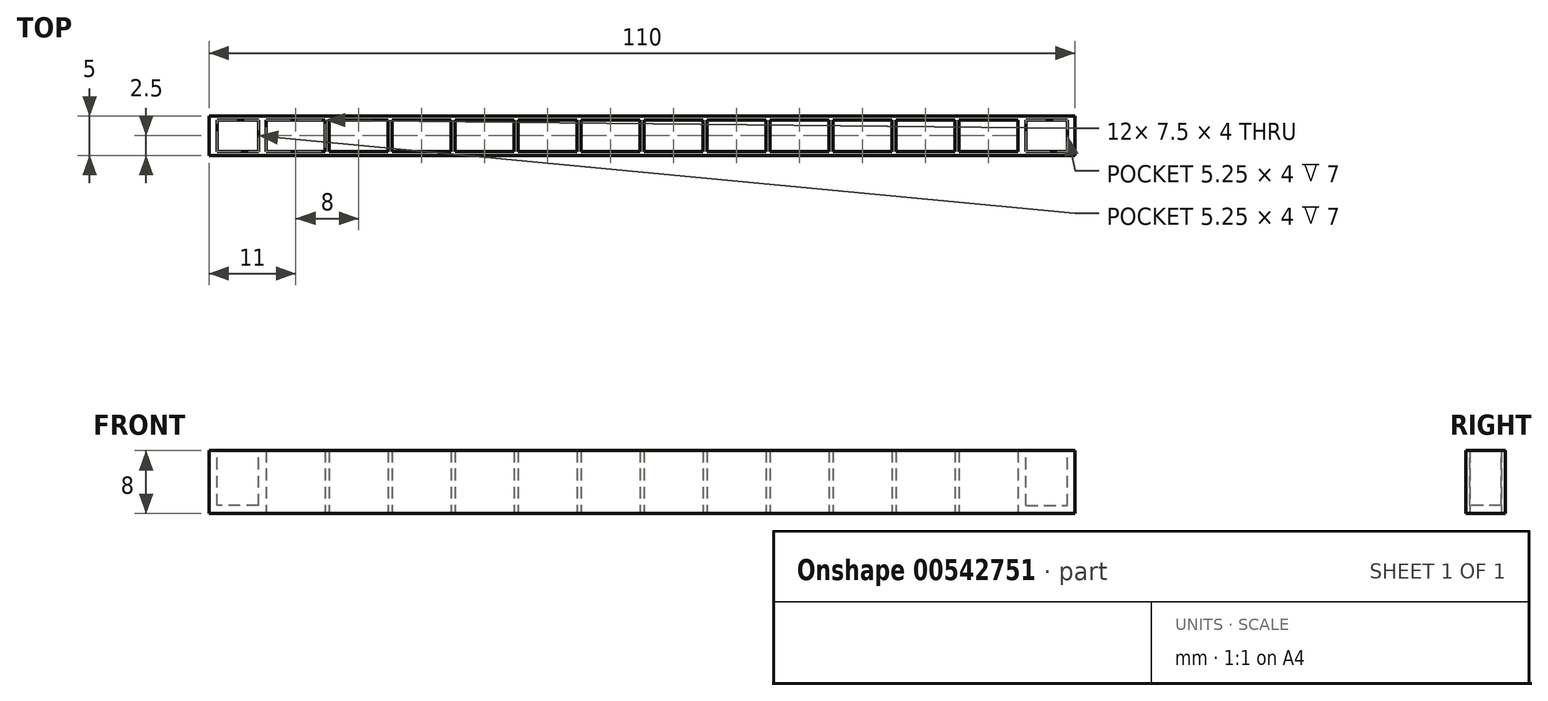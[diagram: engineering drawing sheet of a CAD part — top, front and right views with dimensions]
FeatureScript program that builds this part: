
annotation { "Feature Type Name" : "Feature", "Feature Type Description" : "" }
export const myFeature = defineFeature(function(context is Context, id is Id, definition is map)
    precondition{}
    {
        {
            var Q0;
            Q0=qCreatedBy(makeId("Top.planeOp"),FACE);
            var sketch = newSketch(context, id + "F0", { "sketchPlane" : qUnion([Q0])});
            skLineSegment(sketch, "E0.bottom", {"start": v(-47.75, 2) * mm, "end": v(-40.25, 2) * mm});
            skLineSegment(sketch, "E0.top", {"start": v(-47.75, -2) * mm, "end": v(-40.25, -2) * mm});
            skLineSegment(sketch, "E0.left", {"start": v(-47.75, 2) * mm, "end": v(-47.75, -2) * mm});
            skLineSegment(sketch, "E0.right", {"start": v(-40.25, 2) * mm, "end": v(-40.25, -2) * mm});
            skLineSegment(sketch, "E1.1.0.0", {"start": v(-39.75, 2) * mm, "end": v(-39.75, -2) * mm});
            skLineSegment(sketch, "E1.1.0.1", {"start": v(-39.75, 2) * mm, "end": v(-32.25, 2) * mm});
            skLineSegment(sketch, "E1.1.0.2", {"start": v(-32.25, 2) * mm, "end": v(-32.25, -2) * mm});
            skLineSegment(sketch, "E1.1.0.3", {"start": v(-39.75, -2) * mm, "end": v(-32.25, -2) * mm});
            skLineSegment(sketch, "E1.2.0.0", {"start": v(-31.75, 2) * mm, "end": v(-31.75, -2) * mm});
            skLineSegment(sketch, "E1.2.0.1", {"start": v(-31.75, 2) * mm, "end": v(-24.25, 2) * mm});
            skLineSegment(sketch, "E1.2.0.2", {"start": v(-24.25, 2) * mm, "end": v(-24.25, -2) * mm});
            skLineSegment(sketch, "E1.2.0.3", {"start": v(-31.75, -2) * mm, "end": v(-24.25, -2) * mm});
            skLineSegment(sketch, "E1.3.0.0", {"start": v(-23.75, 2) * mm, "end": v(-23.75, -2) * mm});
            skLineSegment(sketch, "E1.3.0.1", {"start": v(-23.75, 2) * mm, "end": v(-16.25, 2) * mm});
            skLineSegment(sketch, "E1.3.0.2", {"start": v(-16.25, 2) * mm, "end": v(-16.25, -2) * mm});
            skLineSegment(sketch, "E1.3.0.3", {"start": v(-23.75, -2) * mm, "end": v(-16.25, -2) * mm});
            skLineSegment(sketch, "E1.4.0.0", {"start": v(-15.75, 2) * mm, "end": v(-15.75, -2) * mm});
            skLineSegment(sketch, "E1.4.0.1", {"start": v(-15.75, 2) * mm, "end": v(-8.25, 2) * mm});
            skLineSegment(sketch, "E1.4.0.2", {"start": v(-8.25, 2) * mm, "end": v(-8.25, -2) * mm});
            skLineSegment(sketch, "E1.4.0.3", {"start": v(-15.75, -2) * mm, "end": v(-8.25, -2) * mm});
            skLineSegment(sketch, "E1.5.0.0", {"start": v(-7.75, 2) * mm, "end": v(-7.75, -2) * mm});
            skLineSegment(sketch, "E1.5.0.1", {"start": v(-7.75, 2) * mm, "end": v(-0.25, 2) * mm});
            skLineSegment(sketch, "E1.5.0.2", {"start": v(-0.25, 2) * mm, "end": v(-0.25, -2) * mm});
            skLineSegment(sketch, "E1.5.0.3", {"start": v(-7.75, -2) * mm, "end": v(-0.25, -2) * mm});
            skLineSegment(sketch, "E1.6.0.0", {"start": v(0.25, 2) * mm, "end": v(0.25, -2) * mm});
            skLineSegment(sketch, "E1.6.0.1", {"start": v(0.25, 2) * mm, "end": v(7.75, 2) * mm});
            skLineSegment(sketch, "E1.6.0.2", {"start": v(7.75, 2) * mm, "end": v(7.75, -2) * mm});
            skLineSegment(sketch, "E1.6.0.3", {"start": v(0.25, -2) * mm, "end": v(7.75, -2) * mm});
            skLineSegment(sketch, "E1.7.0.0", {"start": v(8.25, 2) * mm, "end": v(8.25, -2) * mm});
            skLineSegment(sketch, "E1.7.0.1", {"start": v(8.25, 2) * mm, "end": v(15.75, 2) * mm});
            skLineSegment(sketch, "E1.7.0.2", {"start": v(15.75, 2) * mm, "end": v(15.75, -2) * mm});
            skLineSegment(sketch, "E1.7.0.3", {"start": v(8.25, -2) * mm, "end": v(15.75, -2) * mm});
            skLineSegment(sketch, "E1.8.0.0", {"start": v(16.25, 2) * mm, "end": v(16.25, -2) * mm});
            skLineSegment(sketch, "E1.8.0.1", {"start": v(16.25, 2) * mm, "end": v(23.75, 2) * mm});
            skLineSegment(sketch, "E1.8.0.2", {"start": v(23.75, 2) * mm, "end": v(23.75, -2) * mm});
            skLineSegment(sketch, "E1.8.0.3", {"start": v(16.25, -2) * mm, "end": v(23.75, -2) * mm});
            skLineSegment(sketch, "E1.9.0.0", {"start": v(24.25, 2) * mm, "end": v(24.25, -2) * mm});
            skLineSegment(sketch, "E1.9.0.1", {"start": v(24.25, 2) * mm, "end": v(31.75, 2) * mm});
            skLineSegment(sketch, "E1.9.0.2", {"start": v(31.75, 2) * mm, "end": v(31.75, -2) * mm});
            skLineSegment(sketch, "E1.9.0.3", {"start": v(24.25, -2) * mm, "end": v(31.75, -2) * mm});
            skLineSegment(sketch, "E1.10.0.0", {"start": v(32.25, 2) * mm, "end": v(32.25, -2) * mm});
            skLineSegment(sketch, "E1.10.0.1", {"start": v(32.25, 2) * mm, "end": v(39.75, 2) * mm});
            skLineSegment(sketch, "E1.10.0.2", {"start": v(39.75, 2) * mm, "end": v(39.75, -2) * mm});
            skLineSegment(sketch, "E1.10.0.3", {"start": v(32.25, -2) * mm, "end": v(39.75, -2) * mm});
            skLineSegment(sketch, "E1.11.0.0", {"start": v(40.25, 2) * mm, "end": v(40.25, -2) * mm});
            skLineSegment(sketch, "E1.11.0.1", {"start": v(40.25, 2) * mm, "end": v(47.75, 2) * mm});
            skLineSegment(sketch, "E1.11.0.2", {"start": v(47.75, 2) * mm, "end": v(47.75, -2) * mm});
            skLineSegment(sketch, "E1.11.0.3", {"start": v(40.25, -2) * mm, "end": v(47.75, -2) * mm});
            skLineSegment(sketch, "E1.direction1", {"start": v(-47.75, -2) * mm, "end": v(-39.75, -2) * mm, "construction": true});
            skLineSegment(sketch, "E2.bottom", {"start": v(-55, 2.5) * mm, "end": v(55, 2.5) * mm});
            skLineSegment(sketch, "E2.top", {"start": v(-55, -2.5) * mm, "end": v(55, -2.5) * mm});
            skLineSegment(sketch, "E2.left", {"start": v(-55, 2.5) * mm, "end": v(-55, -2.5) * mm});
            skLineSegment(sketch, "E2.right", {"start": v(55, 2.5) * mm, "end": v(55, -2.5) * mm});
            skSolve(sketch);
        }
        {
            var Q0;
            Q0=makeQuery(id+"F0.imprint","IMPRINT",FACE,{"disambiguationData":[TD([[makeQuery(id+"F0.imprint","IMPRINT",EDGE,{"derivedFrom":sQuery(id+"F0.wireOp",EDGE,"E0.bottom")}),1.0]])]});
            extrude(context, id + "F1", {"entities" : qUnion([Q0]), "depth" : 8 * mm, "offsetDistance" : 25 * mm});
        }
        {
            var Q0;
            Q0=makeQuery(id+"F1.opExtrude","CAP_FACE",FACE,{"disambiguationData":[OSD([sQuery(id+"F0.wireOp",EDGE,"E0.bottom"),sQuery(id+"F0.wireOp",EDGE,"E0.top"),sQuery(id+"F0.wireOp",EDGE,"E0.left"),sQuery(id+"F0.wireOp",EDGE,"E0.right"),sQuery(id+"F0.wireOp",EDGE,"E1.1.0.0"),sQuery(id+"F0.wireOp",EDGE,"E1.1.0.1"),sQuery(id+"F0.wireOp",EDGE,"E1.1.0.2"),sQuery(id+"F0.wireOp",EDGE,"E1.1.0.3"),sQuery(id+"F0.wireOp",EDGE,"E1.2.0.0"),sQuery(id+"F0.wireOp",EDGE,"E1.2.0.1"),sQuery(id+"F0.wireOp",EDGE,"E1.2.0.2"),sQuery(id+"F0.wireOp",EDGE,"E1.2.0.3"),sQuery(id+"F0.wireOp",EDGE,"E1.3.0.0"),sQuery(id+"F0.wireOp",EDGE,"E1.3.0.1"),sQuery(id+"F0.wireOp",EDGE,"E1.3.0.2"),sQuery(id+"F0.wireOp",EDGE,"E1.3.0.3"),sQuery(id+"F0.wireOp",EDGE,"E1.4.0.0"),sQuery(id+"F0.wireOp",EDGE,"E1.4.0.1"),sQuery(id+"F0.wireOp",EDGE,"E1.4.0.2"),sQuery(id+"F0.wireOp",EDGE,"E1.4.0.3"),sQuery(id+"F0.wireOp",EDGE,"E1.5.0.0"),sQuery(id+"F0.wireOp",EDGE,"E1.5.0.1"),sQuery(id+"F0.wireOp",EDGE,"E1.5.0.2"),sQuery(id+"F0.wireOp",EDGE,"E1.5.0.3"),sQuery(id+"F0.wireOp",EDGE,"E1.6.0.0"),sQuery(id+"F0.wireOp",EDGE,"E1.6.0.1"),sQuery(id+"F0.wireOp",EDGE,"E1.6.0.2"),sQuery(id+"F0.wireOp",EDGE,"E1.6.0.3"),sQuery(id+"F0.wireOp",EDGE,"E1.7.0.0"),sQuery(id+"F0.wireOp",EDGE,"E1.7.0.1"),sQuery(id+"F0.wireOp",EDGE,"E1.7.0.2"),sQuery(id+"F0.wireOp",EDGE,"E1.7.0.3"),sQuery(id+"F0.wireOp",EDGE,"E1.8.0.0"),sQuery(id+"F0.wireOp",EDGE,"E1.8.0.1"),sQuery(id+"F0.wireOp",EDGE,"E1.8.0.2"),sQuery(id+"F0.wireOp",EDGE,"E1.8.0.3"),sQuery(id+"F0.wireOp",EDGE,"E1.9.0.0"),sQuery(id+"F0.wireOp",EDGE,"E1.9.0.1"),sQuery(id+"F0.wireOp",EDGE,"E1.9.0.2"),sQuery(id+"F0.wireOp",EDGE,"E1.9.0.3"),sQuery(id+"F0.wireOp",EDGE,"E1.10.0.0"),sQuery(id+"F0.wireOp",EDGE,"E1.10.0.1"),sQuery(id+"F0.wireOp",EDGE,"E1.10.0.2"),sQuery(id+"F0.wireOp",EDGE,"E1.10.0.3"),sQuery(id+"F0.wireOp",EDGE,"E1.11.0.0"),sQuery(id+"F0.wireOp",EDGE,"E1.11.0.1"),sQuery(id+"F0.wireOp",EDGE,"E1.11.0.2"),sQuery(id+"F0.wireOp",EDGE,"E1.11.0.3"),sQuery(id+"F0.wireOp",EDGE,"E2.bottom"),sQuery(id+"F0.wireOp",EDGE,"E2.top"),sQuery(id+"F0.wireOp",EDGE,"E2.left"),sQuery(id+"F0.wireOp",EDGE,"E2.right")])],"isStart":false});
            var sketch = newSketch(context, id + "F2", { "sketchPlane" : qUnion([Q0])});
            skLineSegment(sketch, "E3.bottom", {"start": v(-48.75, 2) * mm, "end": v(-54, 2) * mm});
            skLineSegment(sketch, "E3.top", {"start": v(-48.75, -2) * mm, "end": v(-54, -2) * mm});
            skLineSegment(sketch, "E3.left", {"start": v(-48.75, 2) * mm, "end": v(-48.75, -2) * mm});
            skLineSegment(sketch, "E3.right", {"start": v(-54, 2) * mm, "end": v(-54, -2) * mm});
            skLineSegment(sketch, "E4.bottom", {"start": v(48.75, 2) * mm, "end": v(54, 2) * mm});
            skLineSegment(sketch, "E4.top", {"start": v(48.75, -2) * mm, "end": v(54, -2) * mm});
            skLineSegment(sketch, "E4.left", {"start": v(48.75, 2) * mm, "end": v(48.75, -2) * mm});
            skLineSegment(sketch, "E4.right", {"start": v(54, 2) * mm, "end": v(54, -2) * mm});
            skSolve(sketch);
        }
        {
            var Q0;
            Q0=makeQuery(id+"F2.imprint","IMPRINT",FACE,{"disambiguationData":[TD([[makeQuery(id+"F2.imprint","IMPRINT",EDGE,{"derivedFrom":sQuery(id+"F2.wireOp",EDGE,"E3.bottom")}),1.0]])]});
            var Q1;
            Q1=makeQuery(id+"F2.imprint","IMPRINT",FACE,{"disambiguationData":[TD([[makeQuery(id+"F2.imprint","IMPRINT",EDGE,{"derivedFrom":sQuery(id+"F2.wireOp",EDGE,"E4.bottom")}),-1.0]])]});
            extrude(context, id + "F3", {"entities" : qUnion([Q0, Q1]), "operationType" : NewBodyOperationType.REMOVE, "oppositeDirection" : true, "depth" : 7 * mm, "offsetDistance" : 25 * mm});
        }
    });
